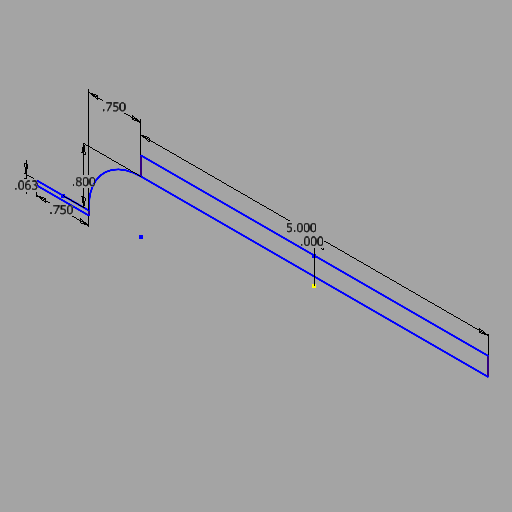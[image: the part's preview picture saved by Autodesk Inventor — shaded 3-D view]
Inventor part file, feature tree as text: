
AUTODESK INVENTOR PART (.ipt)
format: ipt  version: 2025.1 (Build 291241000, 241)  size: 224,768 bytes
history: native  units: in
note: dims shown in document units (in); Inventor stores cm internally (conversion verified against a paired STEP export)
features: sheet_metal_op x12, other x10, sketch x9, extrude x2, mirror x2, chamfer x2
ambient origin geometry x8: Origin, YZ Plane, XZ Plane, XY Plane, X Axis, Y Axis, Z Axis, Center Point
bodies: Solid1 (feature_tree)
feature tree (37):
  extrude  "Top"  Depth=1.375in
  other  "Flange; 1"
  other  "Flange; 2"
  other  "Flange; 3"
  other  "Flange; 4"
  other  "Flange; 5"
  extrude  "Hole"  Depth=0.063in
  mirror  "Mirror; 1"
  mirror  "Mirror; 2"
  chamfer  "Corner Round; 1"
  chamfer  "Corner Round; 2"
  sheet_metal_op  "Unfold2"
  sheet_metal_op  "Unfold3"
  sketch  "Sketch17"  dims[d13=0.063in d14=0.063in d39=0.6875in d40=2.0in d78=0.063in d79=0.0315in d80=0.126in d81=0.063in d82=0.3438in d83=0.1718in d84=0.063in d85=0.252in d86=0.063in d87=0.063in d88=0.063in d89=0.0315in d90=0.126in d91=0.063in d92=0.3438in d93=0.1718in d94=0.063in d95=0.252in d96=0.063in d97=0.063in d98=0.063in d99=0.0315in d100=0.126in d101=0.063in d102=0.7188in d103=0.1374in d104=0.063in d105=0.252in d106=0.063in d107=0.063in d108=0.063in d109=0.0315in d110=0.126in d111=0.063in d112=0.75in d113=90.0deg d114=0.063in d115=0.252in d116=0.063in d117=0.063in d118=0.25in d119=0.3435in d120=0.687in d121=1.375in d122=0.6875in d123=0.063in d124=0.0in d125=0.063in d126=0.0315in d127=0.126in d128=0.063in d129=0.6804in d130=0.0315in d131=0.0158in d132=0.5in d133=0.05in d134=0.0625in d135=0.0in d136=5.0in d138=0.8in d139=0.75in d140=0.75in]
  sketch  "Sketch1"  dims[d0=4.0in d1=1.375in]
  sketch  "Sketch2"  dims[d2=0.063in d3=0.0in d4=0.063in]
  other  "Plate1"
  sheet_metal_op  "Bend1"
  sheet_metal_op  "Corner1"
  sketch  "Sketch10"  dims[d5=0.063in]
  other  "Plate6"
  sheet_metal_op  "Bend6"
  sheet_metal_op  "Corner6"
  sketch  "Sketch11"  dims[d6=0.0315in]
  other  "Plate7"
  sheet_metal_op  "Bend7"
  sheet_metal_op  "Corner7"
  sketch  "Sketch12"  dims[d7=0.126in]
  other  "Plate8"
  sheet_metal_op  "Bend8"
  sheet_metal_op  "Corner8"
  sketch  "Sketch13"  dims[d8=0.063in]
  other  "Plate9"
  sheet_metal_op  "Bend9"
  sheet_metal_op  "Corner9"
  sketch  "Sketch15"  dims[d9=0.3438in d10=0.1374in d11=0.063in]
  sketch  "Sketch16"  dims[d12=0.252in]
